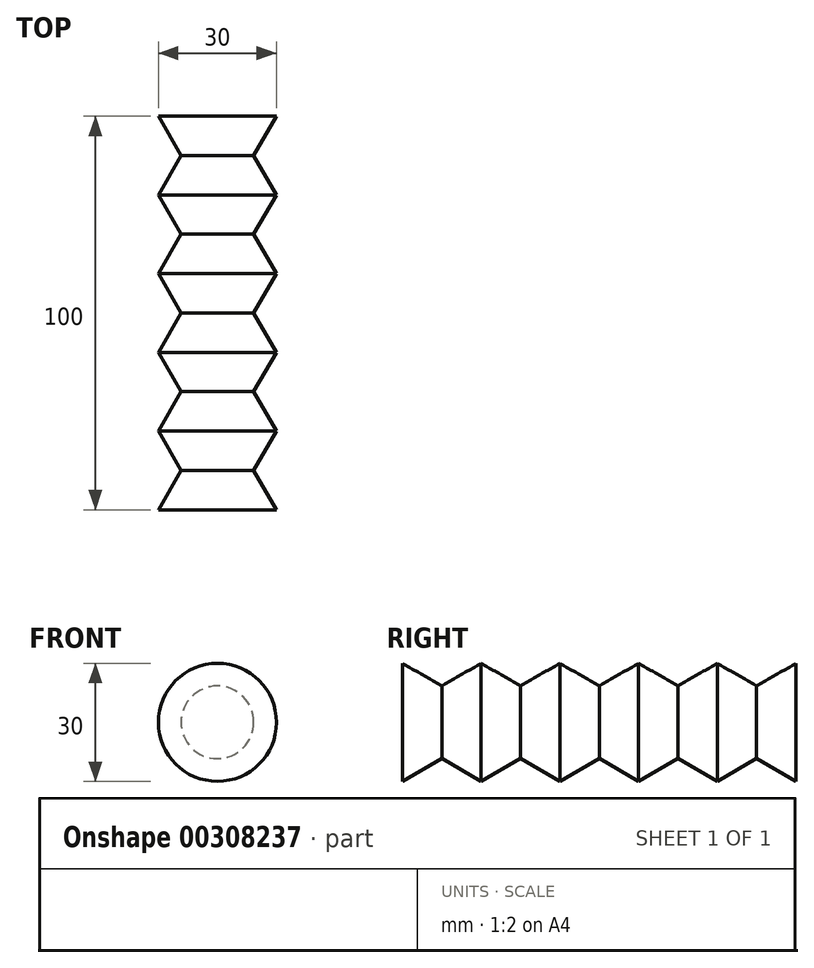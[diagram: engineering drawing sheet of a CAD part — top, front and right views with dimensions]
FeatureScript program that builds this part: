
annotation { "Feature Type Name" : "Feature", "Feature Type Description" : "" }
export const myFeature = defineFeature(function(context is Context, id is Id, definition is map)
    precondition{}
    {
        {
            var Q0;
            Q0=qCreatedBy(makeId("Top.planeOp"),FACE);
            var sketch = newSketch(context, id + "F0", { "sketchPlane" : qUnion([Q0])});
            skLineSegment(sketch, "E0", {"start": v(0, 22.02) * mm, "end": v(15, 22.02) * mm});
            skLineSegment(sketch, "E1", {"start": v(15, -37.98) * mm, "end": v(9.23, -47.98) * mm});
            skLineSegment(sketch, "E2", {"start": v(9.23, -47.98) * mm, "end": v(15, -57.98) * mm});
            skLineSegment(sketch, "E3", {"start": v(15, -57.98) * mm, "end": v(9.23, -67.98) * mm});
            skLineSegment(sketch, "E4", {"start": v(9.23, -67.98) * mm, "end": v(15, -77.98) * mm});
            skLineSegment(sketch, "E5", {"start": v(15, -77.98) * mm, "end": v(0, -77.98) * mm});
            skLineSegment(sketch, "E6", {"start": v(9.23, 81.52) * mm, "end": v(9.23, -213.43) * mm, "construction": true});
            skLineSegment(sketch, "E7", {"start": v(15, 57.81) * mm, "end": v(15, -184.47) * mm, "construction": true});
            skLineSegment(sketch, "E8", {"start": v(0, 54.62) * mm, "end": v(0, -192.76) * mm, "construction": true});
            skLineSegment(sketch, "E9", {"start": v(15, -37.98) * mm, "end": v(9.23, -27.98) * mm});
            skLineSegment(sketch, "E10", {"start": v(9.23, -27.98) * mm, "end": v(15, -17.98) * mm});
            skLineSegment(sketch, "E11", {"start": v(15, 2.02) * mm, "end": v(9.23, -7.98) * mm});
            skLineSegment(sketch, "E12", {"start": v(9.23, -7.98) * mm, "end": v(15, -17.98) * mm});
            skLineSegment(sketch, "E13", {"start": v(15, 22.02) * mm, "end": v(9.23, 12.02) * mm});
            skLineSegment(sketch, "E14", {"start": v(9.23, 12.02) * mm, "end": v(15, 2.02) * mm});
            skLineSegment(sketch, "E15", {"start": v(0, 22.02) * mm, "end": v(0, -77.98) * mm});
            skSolve(sketch);
        }
        {
            var Q0;
            Q0=makeQuery(id+"F0.imprint","IMPRINT",FACE,{"disambiguationData":[TD([[makeQuery(id+"F0.imprint","IMPRINT",EDGE,{"derivedFrom":sQuery(id+"F0.wireOp",EDGE,"E0")}),-1.0]])]});
            var Q1;
            Q1=sQuery(id+"F0.wireOp",EDGE,"E15");
            revolve(context, id + "F1", {"surfaceOperationType" : NewSurfaceOperationType.NEW, "entities" : qUnion([Q0]), "axis" : qUnion([Q1]), "revolveType" : RevolveType.FULL});
        }
    });
